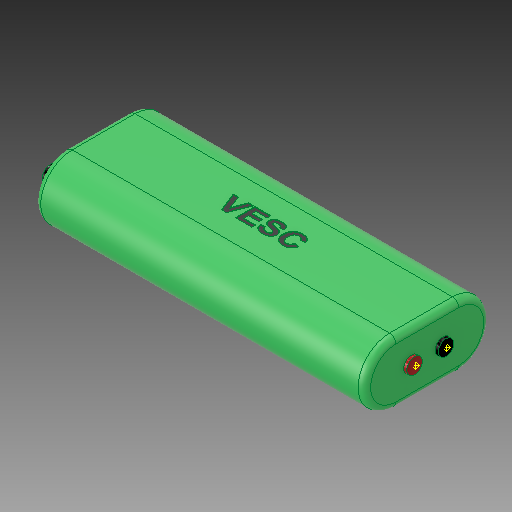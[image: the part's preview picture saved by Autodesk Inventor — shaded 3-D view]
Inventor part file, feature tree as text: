
AUTODESK INVENTOR PART (.ipt)
format: ipt  version: 2019.3 (Build 233278000, 278)  size: 412,160 bytes
history: native  units: mm
features: sketch x9, other x5, extrude x3, fillet x2, emboss x1, chamfer x1
ambient origin geometry x8: Origin, YZ Plane, XZ Plane, XY Plane, X Axis, Y Axis, Z Axis, Center Point
bodies: Solid1 (feature_tree)
feature tree (21):
  extrude  "Extrusion1"  Depth=40.0mm
  emboss  "Emboss1"
  extrude  "Extrusion2"  Depth=2.5mm
  extrude  "Extrusion3"  Depth=0.1mm TaperAngle=0.0deg
  fillet  "Fillet1"  Radius=5.0mm
  fillet  "Fillet2"  Radius=10.0mm
  chamfer  "Chamfer1"  Distance=5.0mm
  sketch  "Sketch5"  dims[d13=5.0mm]
  other  "NEGAITVE"
  sketch  "Sketch6"  dims[d14=5.0mm]
  other  "POSITIVE"
  sketch  "Sketch7"  dims[d15=15.0mm]
  other  "OUT_1"
  sketch  "Sketch8"  dims[d16=15.0mm]
  other  "OUT_2"
  sketch  "Sketch9"  dims[d17=1.0mm d18=0.0mm d19=10.0mm d20=2.0mm d21=0.1mm d22=2.0mm d23=45.0deg]
  other  "OUT_3"
  sketch  "Sketch1"  dims[d0=105.0mm d1=40.0mm]
  sketch  "Sketch2"  dims[d2=20.0mm d3=0.0mm d4=2.5mm]
  sketch  "Sketch3"  dims[d5=2.5mm d6=0.1mm d7=0.0mm d8=5.0mm d9=10.0mm]
  sketch  "Sketch4"  dims[d10=5.0mm d11=5.0mm d12=0.0mm]
